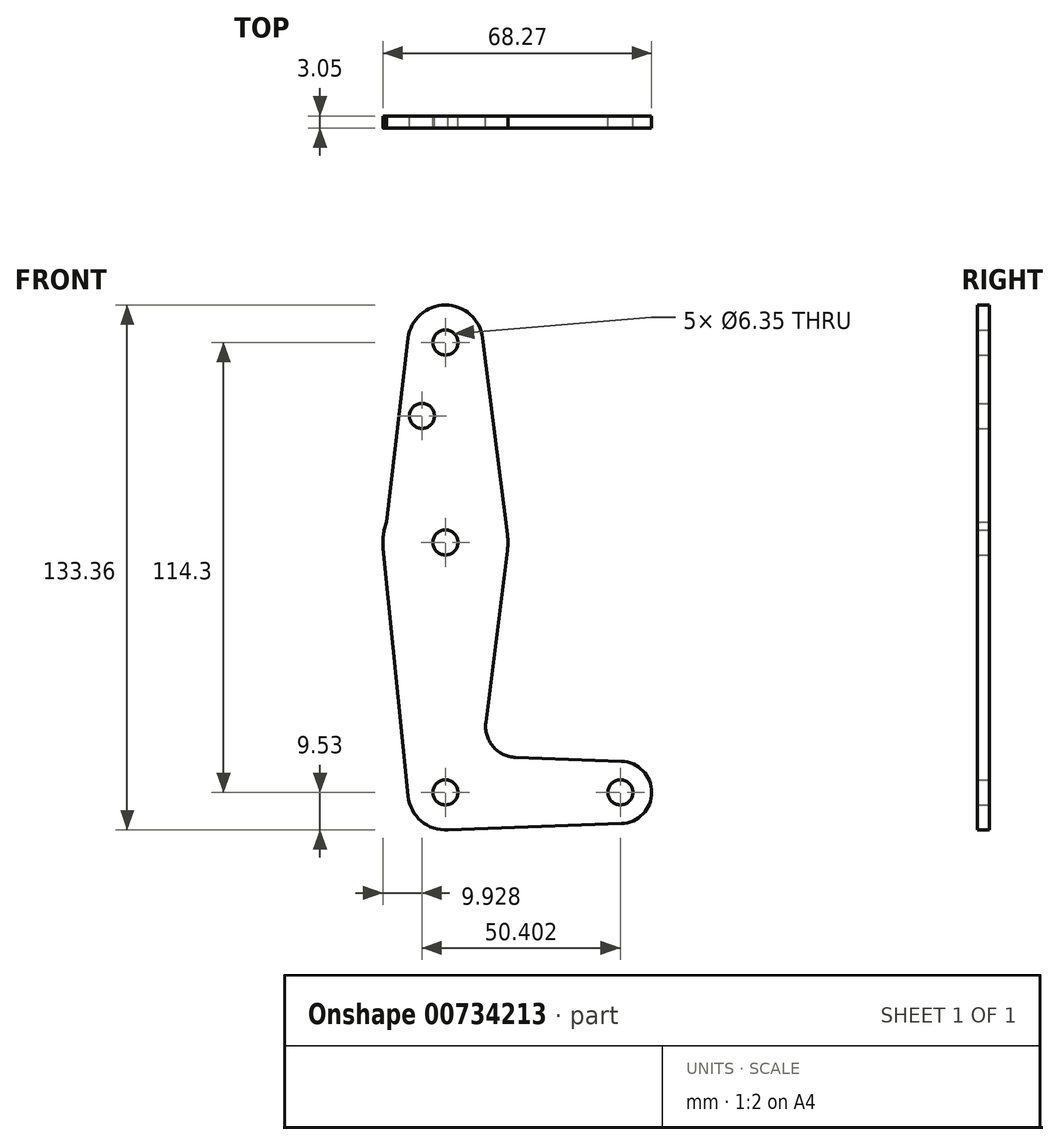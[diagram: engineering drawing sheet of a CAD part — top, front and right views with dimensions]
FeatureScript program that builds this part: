
annotation { "Feature Type Name" : "Feature", "Feature Type Description" : "" }
export const myFeature = defineFeature(function(context is Context, id is Id, definition is map)
    precondition{}
    {
        {
            var Q0;
            Q0=qCreatedBy(makeId("Front.planeOp"),FACE);
            var sketch = newSketch(context, id + "F0", { "sketchPlane" : qUnion([Q0])});
            skLineSegment(sketch, "E0", {"start": v(0, 0) * mm, "end": v(44.45, 0) * mm, "construction": true});
            skLineSegment(sketch, "E1", {"start": v(0, 0) * mm, "end": v(0, 63.5) * mm, "construction": true});
            skLineSegment(sketch, "E2", {"start": v(0, 63.5) * mm, "end": v(0, 114.3) * mm, "construction": true});
            skCircle(sketch, "E3", {"center": v(44.45, 0) * mm, "radius": 7.94 * mm});
            skCircle(sketch, "E4", {"center": v(0, 0) * mm, "radius": 9.53 * mm});
            skCircle(sketch, "E5", {"center": v(0, 114.3) * mm, "radius": 9.53 * mm});
            skCircle(sketch, "E6", {"center": v(0, 63.5) * mm, "radius": 15.88 * mm});
            skLineSegment(sketch, "E7", {"start": v(-9.46, 115.42) * mm, "end": v(-15.8, 61.91) * mm});
            skLineSegment(sketch, "E8", {"start": v(9.45, 115.5) * mm, "end": v(15.75, 65.48) * mm});
            skLineSegment(sketch, "E9", {"start": v(-15.8, 61.91) * mm, "end": v(-9.48, -0.95) * mm});
            skLineSegment(sketch, "E10", {"start": v(15.75, 61.52) * mm, "end": v(10.25, 17.83) * mm});
            skLineSegment(sketch, "E11", {"start": v(17.85, 8.9) * mm, "end": v(44.73, 7.93) * mm});
            skLineSegment(sketch, "E12", {"start": v(0, -9.53) * mm, "end": v(44.73, -7.93) * mm});
            skCircle(sketch, "E13", {"center": v(0, 114.3) * mm, "radius": 3.18 * mm});
            skCircle(sketch, "E14", {"center": v(-5.95, 95.67) * mm, "radius": 3.18 * mm});
            skCircle(sketch, "E15", {"center": v(0, 63.5) * mm, "radius": 3.18 * mm});
            skCircle(sketch, "E16", {"center": v(0, 0) * mm, "radius": 3.18 * mm});
            skCircle(sketch, "E17", {"center": v(44.45, 0) * mm, "radius": 3.18 * mm});
            skArc(sketch, "E18.filletArc", {"start": v(10.25, 17.83) * mm, "mid": v(12.08, 11.69) * mm, "end": v(17.85, 8.9) * mm});
            skSolve(sketch);
        }
        {
            var Q0;
            Q0 = qSketchRegion(id + "F0", true);
            extrude(context, id + "F1", {"entities" : qUnion([Q0]), "depth" : 3.05 * mm, "offsetDistance" : 25.4 * mm});
        }
    });
